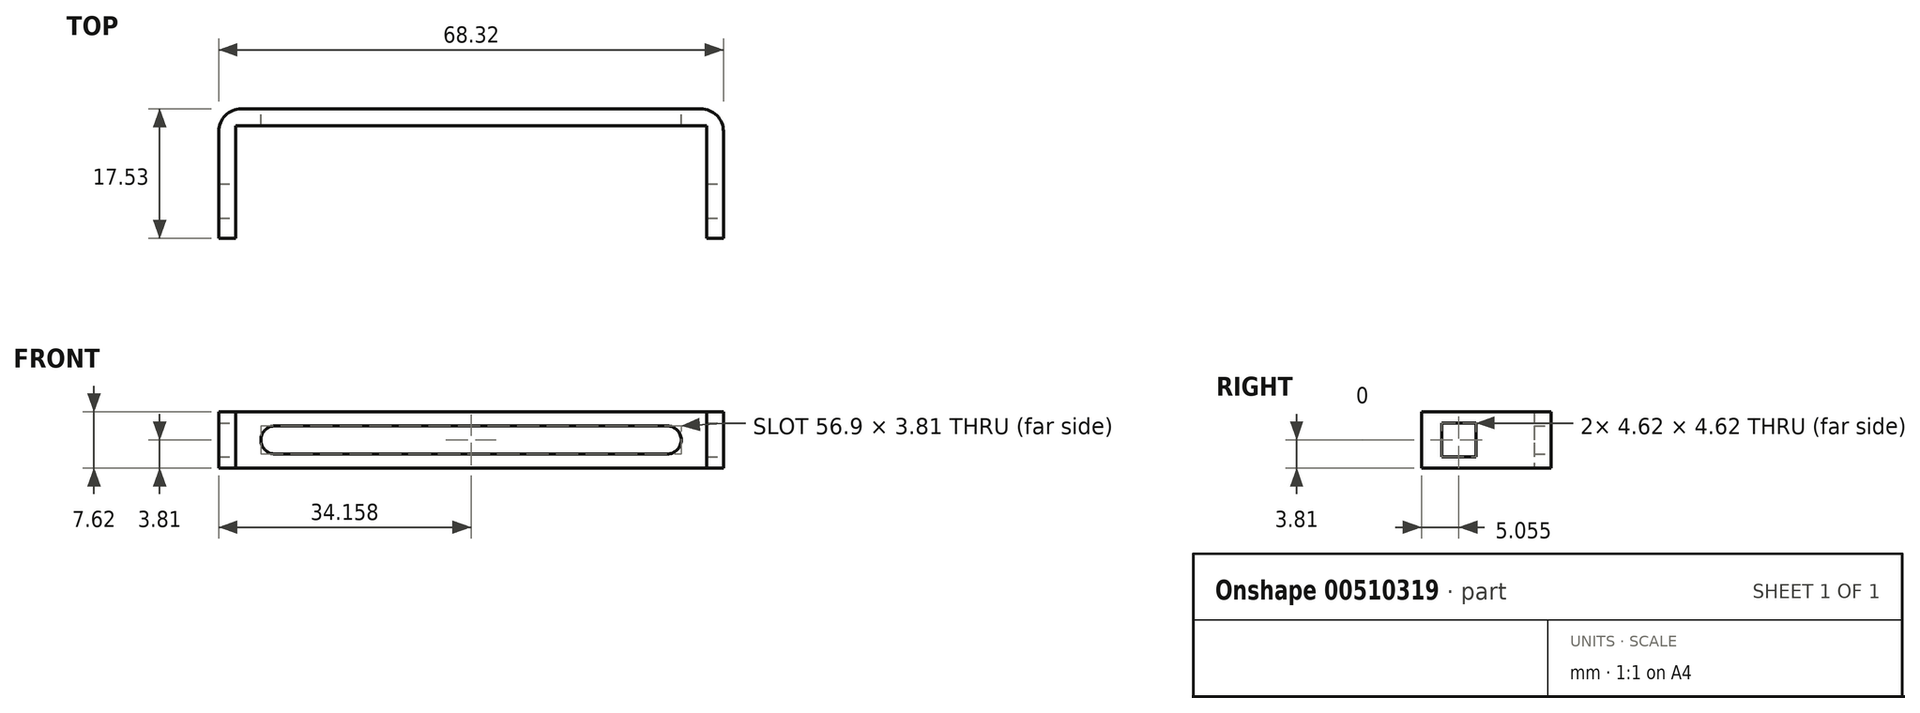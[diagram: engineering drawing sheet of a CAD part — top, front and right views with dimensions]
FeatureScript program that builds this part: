
annotation { "Feature Type Name" : "Feature", "Feature Type Description" : "" }
export const myFeature = defineFeature(function(context is Context, id is Id, definition is map)
    precondition{}
    {
        {
            var Q0;
            Q0=qCreatedBy(makeId("Top.planeOp"),FACE);
            var sketch = newSketch(context, id + "F0", { "sketchPlane" : qUnion([Q0])});
            skLineSegment(sketch, "E0", {"start": v(-30.08, 23.96) * mm, "end": v(33.68, 23.96) * mm});
            skLineSegment(sketch, "E1", {"start": v(-30.08, 23.96) * mm, "end": v(-30.08, 8.72) * mm});
            skLineSegment(sketch, "E2", {"start": v(33.68, 23.96) * mm, "end": v(33.68, 8.72) * mm});
            skLineSegment(sketch, "E3.0", {"start": v(35.96, 26.25) * mm, "end": v(35.96, 8.72) * mm});
            skLineSegment(sketch, "E3.1", {"start": v(-32.36, 26.25) * mm, "end": v(35.96, 26.25) * mm});
            skLineSegment(sketch, "E3.2", {"start": v(-32.36, 26.25) * mm, "end": v(-32.36, 8.72) * mm});
            skLineSegment(sketch, "E4", {"start": v(-30.08, 8.72) * mm, "end": v(-32.36, 8.72) * mm});
            skLineSegment(sketch, "E5", {"start": v(33.68, 8.72) * mm, "end": v(35.96, 8.72) * mm});
            skSolve(sketch);
        }
        {
            var Q0;
            Q0=makeQuery(id+"F0.imprint","IMPRINT",FACE,{"disambiguationData":[TD([[makeQuery(id+"F0.imprint","IMPRINT",EDGE,{"derivedFrom":sQuery(id+"F0.wireOp",EDGE,"E0")}),1.0]])]});
            extrude(context, id + "F1", {"entities" : qUnion([Q0]), "depth" : 7.62 * mm});
        }
        {
            var Q0;
            Q0=makeQuery(id+"F1.opExtrude","SWEPT_FACE",FACE,{"disambiguationData":[OSD([sQuery(id+"F0.wireOp",EDGE,"E3.0")])]});
            var sketch = newSketch(context, id + "F2", { "sketchPlane" : qUnion([Q0])});
            skLineSegment(sketch, "E6", {"start": v(8.72, 3.81) * mm, "end": v(26.25, 3.81) * mm, "construction": true});
            skLineSegment(sketch, "E7.bottom", {"start": v(11.46, 1.5) * mm, "end": v(16.09, 1.5) * mm});
            skLineSegment(sketch, "E7.top", {"start": v(11.46, 6.12) * mm, "end": v(16.09, 6.12) * mm});
            skLineSegment(sketch, "E7.left", {"start": v(11.46, 1.5) * mm, "end": v(11.46, 6.12) * mm});
            skLineSegment(sketch, "E7.right", {"start": v(16.09, 1.5) * mm, "end": v(16.09, 6.12) * mm});
            skPoint(sketch, "E7.middle", {"position": v(13.78, 3.81) * mm});
            skSolve(sketch);
        }
        {
            var Q0;
            Q0=makeQuery(id+"F2.imprint","IMPRINT",FACE,{"disambiguationData":[TD([[makeQuery(id+"F2.imprint","IMPRINT",EDGE,{"derivedFrom":sQuery(id+"F2.wireOp",EDGE,"E7.bottom")}),1.0]])]});
            extrude(context, id + "F3", {"entities" : qUnion([Q0]), "operationType" : NewBodyOperationType.REMOVE, "oppositeDirection" : true, "depth" : 86.1 * mm});
        }
        {
            var Q0;
            Q0=makeQuery(id+"F1.opExtrude","SWEPT_FACE",FACE,{"disambiguationData":[OSD([sQuery(id+"F0.wireOp",EDGE,"E3.1")])]});
            var sketch = newSketch(context, id + "F4", { "sketchPlane" : qUnion([Q0])});
            skLineSegment(sketch, "E8", {"start": v(-35.96, 3.81) * mm, "end": v(32.36, 3.81) * mm, "construction": true});
            skLineSegment(sketch, "E9", {"start": v(-1.8, 7.62) * mm, "end": v(-1.8, 0) * mm, "construction": true});
            skPoint(sketch, "E10", {"position": v(-28.34, 3.81) * mm});
            skArc(sketch, "E11", {"start": v(-28.34, 5.72) * mm, "mid": v(-30.25, 3.81) * mm, "end": v(-28.34, 1.9) * mm});
            skLineSegment(sketch, "E12", {"start": v(-28.34, 5.72) * mm, "end": v(-28.34, 1.9) * mm});
            skArc(sketch, "E13", {"start": v(24.74, 1.9) * mm, "mid": v(26.65, 3.8) * mm, "end": v(24.74, 5.71) * mm});
            skLineSegment(sketch, "E14", {"start": v(-28.34, 5.72) * mm, "end": v(24.74, 5.71) * mm});
            skLineSegment(sketch, "E15", {"start": v(-28.34, 1.9) * mm, "end": v(24.74, 1.9) * mm});
            skSolve(sketch);
        }
        {
            var Q0;
            Q0=makeQuery(id+"F4.imprint","IMPRINT",FACE,{"disambiguationData":[TD([[makeQuery(id+"F4.imprint","IMPRINT",EDGE,{"derivedFrom":sQuery(id+"F4.wireOp",EDGE,"E12")}),1.0]])]});
            var Q1;
            Q1=makeQuery(id+"F4.imprint","IMPRINT",FACE,{"disambiguationData":[TD([[makeQuery(id+"F4.imprint","IMPRINT",EDGE,{"derivedFrom":sQuery(id+"F4.wireOp",EDGE,"E11")}),1.0]])]});
            extrude(context, id + "F5", {"entities" : qUnion([Q0, Q1]), "operationType" : NewBodyOperationType.REMOVE, "oppositeDirection" : true, "depth" : 25.4 * mm});
        }
        {
            var Q0;
            Q0=makeQuery(id+"F1.opExtrude","SWEPT_EDGE",EDGE,{"disambiguationData":[OSD([sQuery(id+"F0.wireOp",EDGE,"E3.0"),sQuery(id+"F0.wireOp",EDGE,"E3.1")])]});
            var Q1;
            Q1=makeQuery(id+"F1.opExtrude","SWEPT_EDGE",EDGE,{"disambiguationData":[OSD([sQuery(id+"F0.wireOp",EDGE,"E3.1"),sQuery(id+"F0.wireOp",EDGE,"E3.2")])]});
            fillet(context, id + "F6", {"entities" : qUnion([Q0, Q1]), "radius" : 3.07 * mm, "tangentPropagation" : true, "allowEdgeOverflow" : false});
        }
    });
